# Revit family: Wood_Lockers-Salsbury_Industries-37000_Series-1_Wide_Units
name_source: partatom
category: Specialty Equipment
units: mm (PartAtom-declared; Revit-internal decimal feet)

## family parameters
Always vertical = Yes
Classification Number = 23.40.00.00
Cut with Voids When Loaded = No
Enable Cutting in Views = No
Maintain Annotation Orientation = No
Part Type = Normal
Room Calculation Point = No
Round Connector Dimension = Use Diameter
Shared = No
Work Plane-Based = No

## types (12) — shared parameters
Assembly Code = C1030310
Building Codes = https://www.lockers.com
Construction Details = https://www.lockers.com
Default Elevation = 0.000"
Door Trim = Rubber Trim - Salsbury Finish - Textured
Green Building-LEED = https://www.arcat.com
Hardware = Aluminum - Salsbury Finish - Black Satin
Installation-Fabrication = https://www.lockers.com
Keynote = 10 51 00
Manufacturer = Salsbury Industries
Manufacturer Fax = 1-800-562-5399
Manufacturer Website = https://www.lockers.com
MasterFormat Code = 10 51 23
MasterFormat Title = Lockers
OmniClass 23 Number = 23.40.00.00
OmniClass 23 Title = Equipment and Furnishings
Primary Structure Materials = Particle Board Industrial Grade - Salsbury Finish - White Melamine Inlay
Product Data = https://www.lockers.com
Revision = R1_2018-10
Sales Information = https://www.lockers.com
Secondary Structure Materials = Particle Board Industrial Grade - Salsbury Finish - Black Melamine Overlay
Specification = https://www.lockers.com
Test Data = https://www.lockers.com
Type Comments = Designer Wood Lockers - Double Tier 'S' Style
URL = www.lockers.com
Unit Trim = Melamine - Salsbury Finish - Black
Width = 12.000"

## per-type parameters (varying)
| type | Base | Base Height | Depth | Description | Door Location D1 | Door Location D2 | Individual Door Height | Model | Sloping Hood Height | Unit Height | Version |
| 37165 | Wood Locker Bases : Base - 12" W x 15" D Lockers | 4.000" | 15.000" | 1 Wide - 6 Feet High - 15 inches Deep - with Base | Wood Locker S-Style Top Doors : Double Tier Top S-Door for Six Foot High Locker | Wood Locker S-Style Bottom Doors : Double Tier Bottom S-Door for Six Foot High Locker | 42.062" | 37165 | 5.743" | 72.000" | 2.0 (07/14/17) |
| 37165 - without Base | Wood Locker Bases : None | 0.000" | 15.000" | 1 Wide - 6 Feet High - 15 inches Deep - without Base | Wood Locker S-Style Top Doors : Double Tier Top S-Door for Six Foot High Locker | Wood Locker S-Style Bottom Doors : Double Tier Bottom S-Door for Six Foot High Locker | 42.062" | 37165 without Base | 5.743" | 72.000" | 2.0  (07/14/17) |
| 37168 | Wood Locker Bases : Base - 12" W x 18" D Lockers | 4.000" | 18.000" | 1 Wide - 6 Feet High - 18 inches Deep - with Base | Wood Locker S-Style Top Doors : Double Tier Top S-Door for Six Foot High Locker | Wood Locker S-Style Bottom Doors : Double Tier Bottom S-Door for Six Foot High Locker | 42.062" | 37168 | 6.868" | 72.000" | 2.0 (07/14/17) |
| 37168 - without Base | Wood Locker Bases : None | 0.000" | 18.000" | 1 Wide - 6 Feet High - 18 inches Deep - without Base | Wood Locker S-Style Top Doors : Double Tier Top S-Door for Six Foot High Locker | Wood Locker S-Style Bottom Doors : Double Tier Bottom S-Door for Six Foot High Locker | 42.062" | 37168 without Base | 6.868" | 72.000" | 2.0 (07/14/17) |
| 37161 | Wood Locker Bases : Base - 12" W x 21" D Lockers | 4.000" | 21.000" | 1 Wide - 6 Feet High - 21 inches Deep - with Base | Wood Locker S-Style Top Doors : Double Tier Top S-Door for Six Foot High Locker | Wood Locker S-Style Bottom Doors : Double Tier Bottom S-Door for Six Foot High Locker | 42.062" | 37161 | 7.993" | 72.000" | 2.0 (07/14/17) |
| 37161 - without Base | Wood Locker Bases : None | 0.000" | 21.000" | 1 Wide - 6 Feet High - 21 inches Deep - without Base | Wood Locker S-Style Top Doors : Double Tier Top S-Door for Six Foot High Locker | Wood Locker S-Style Bottom Doors : Double Tier Bottom S-Door for Six Foot High Locker | 42.062" | 37161 without Base | 7.993" | 72.000" | 2.0 (07/14/17) |
| 37155 | Wood Locker Bases : Base - 12" W x 15" D Lockers | 4.000" | 15.000" | 1 Wide - 5 Feet High - 15 inches Deep - with Base | Wood Locker S-Style Top Doors : Double Tier Top S-Door for Five Foot High Locker | Wood Locker S-Style Bottom Doors : Double Tier Bottom S-Door for Five Foot High Locker | 36.062" | 37155 | 5.743" | 60.000" | 2.0 (07/14/17) |
| 37155 - without Base | Wood Locker Bases : None | 0.000" | 15.000" | 1 Wide - 5 Feet High - 15 inches Deep - without Base | Wood Locker S-Style Top Doors : Double Tier Top S-Door for Five Foot High Locker | Wood Locker S-Style Bottom Doors : Double Tier Bottom S-Door for Five Foot High Locker | 36.062" | 37155 without Base | 5.743" | 60.000" | 2.0 (07/14/17) |
| 37158 | Wood Locker Bases : Base - 12" W x 18" D Lockers | 4.000" | 18.000" | 1 Wide - 5 Feet High - 18 inches Deep - with Base | Wood Locker S-Style Top Doors : Double Tier Top S-Door for Five Foot High Locker | Wood Locker S-Style Bottom Doors : Double Tier Bottom S-Door for Five Foot High Locker | 36.062" | 37158 | 6.868" | 60.000" | 2.0 (07/14/17) |
| 37158 - without Base | Wood Locker Bases : None | 0.000" | 18.000" | 1 Wide - 5 Feet High - 18 inches Deep - without Base | Wood Locker S-Style Top Doors : Double Tier Top S-Door for Five Foot High Locker | Wood Locker S-Style Bottom Doors : Double Tier Bottom S-Door for Five Foot High Locker | 36.062" | 37158 without Base | 6.868" | 60.000" | 2.0 (07/14/17) |
| 37151 | Wood Locker Bases : Base - 12" W x 21" D Lockers | 4.000" | 21.000" | 1 Wide - 5 Feet High - 21 inches Deep - with Base | Wood Locker S-Style Top Doors : Double Tier Top S-Door for Five Foot High Locker | Wood Locker S-Style Bottom Doors : Double Tier Bottom S-Door for Five Foot High Locker | 36.062" | 37151 | 7.993" | 60.000" | 2.0 (07/14/17) |
| 37151 - without Base | Wood Locker Bases : None | 0.000" | 21.000" | 1 Wide - 5 Feet High - 21 inches Deep - without Base | Wood Locker S-Style Top Doors : Double Tier Top S-Door for Five Foot High Locker | Wood Locker S-Style Bottom Doors : Double Tier Bottom S-Door for Five Foot High Locker | 36.062" | 37151 without Base | 7.993" | 60.000" | 2.0 (07/14/17) |

## geometry (parser evidence)
native form markers: Sweep x32
no freeform markers — native parametric forms only
